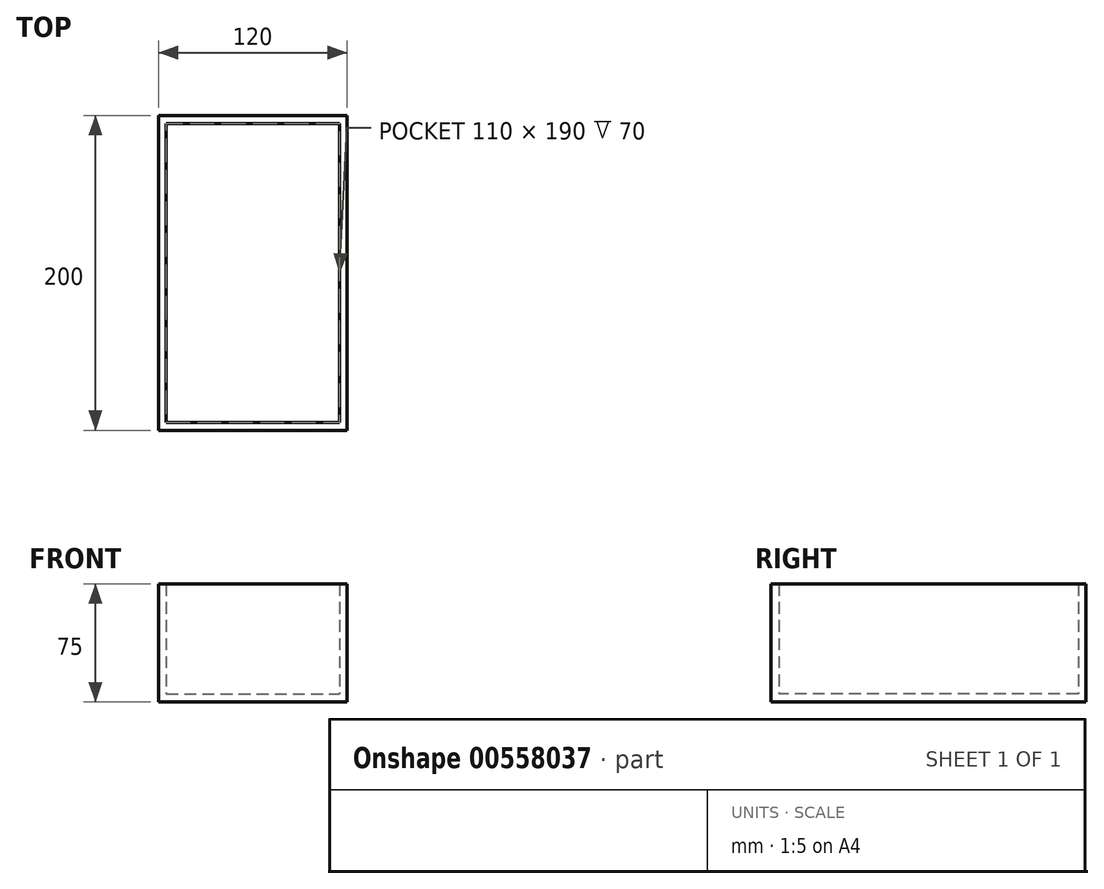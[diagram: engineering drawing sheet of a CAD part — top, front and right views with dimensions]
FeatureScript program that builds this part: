
annotation { "Feature Type Name" : "Feature", "Feature Type Description" : "" }
export const myFeature = defineFeature(function(context is Context, id is Id, definition is map)
    precondition{}
    {
        {
            var Q0;
            Q0=qCreatedBy(makeId("Top.planeOp"),FACE);
            var sketch = newSketch(context, id + "F0", { "sketchPlane" : qUnion([Q0])});
            skLineSegment(sketch, "E0.bottom", {"start": v(-60, 100) * mm, "end": v(60, 100) * mm});
            skLineSegment(sketch, "E0.top", {"start": v(-60, -100) * mm, "end": v(60, -100) * mm});
            skLineSegment(sketch, "E0.left", {"start": v(-60, 100) * mm, "end": v(-60, -100) * mm});
            skLineSegment(sketch, "E0.right", {"start": v(60, 100) * mm, "end": v(60, -100) * mm});
            skLineSegment(sketch, "E1", {"start": v(-60, 0) * mm, "end": v(60, 0) * mm, "construction": true});
            skLineSegment(sketch, "E2", {"start": v(0, 100) * mm, "end": v(0, -100) * mm, "construction": true});
            skSolve(sketch);
        }
        {
            var Q0;
            Q0 = qSketchRegion(id + "F0", true);
            extrude(context, id + "F1", {"entities" : qUnion([Q0]), "depth" : 75 * mm, "offsetDistance" : 25 * mm});
        }
        {
            var Q0;
            Q0=makeQuery(id+"F1.opExtrude","CAP_FACE",FACE,{"disambiguationData":[OSD([sQuery(id+"F0.wireOp",EDGE,"E0.bottom"),sQuery(id+"F0.wireOp",EDGE,"E0.top"),sQuery(id+"F0.wireOp",EDGE,"E0.left"),sQuery(id+"F0.wireOp",EDGE,"E0.right")])],"isStart":false});
            shell(context, id + "F2", {"entities" : qUnion([Q0]), "thickness" : 5 * mm});
        }
    });
